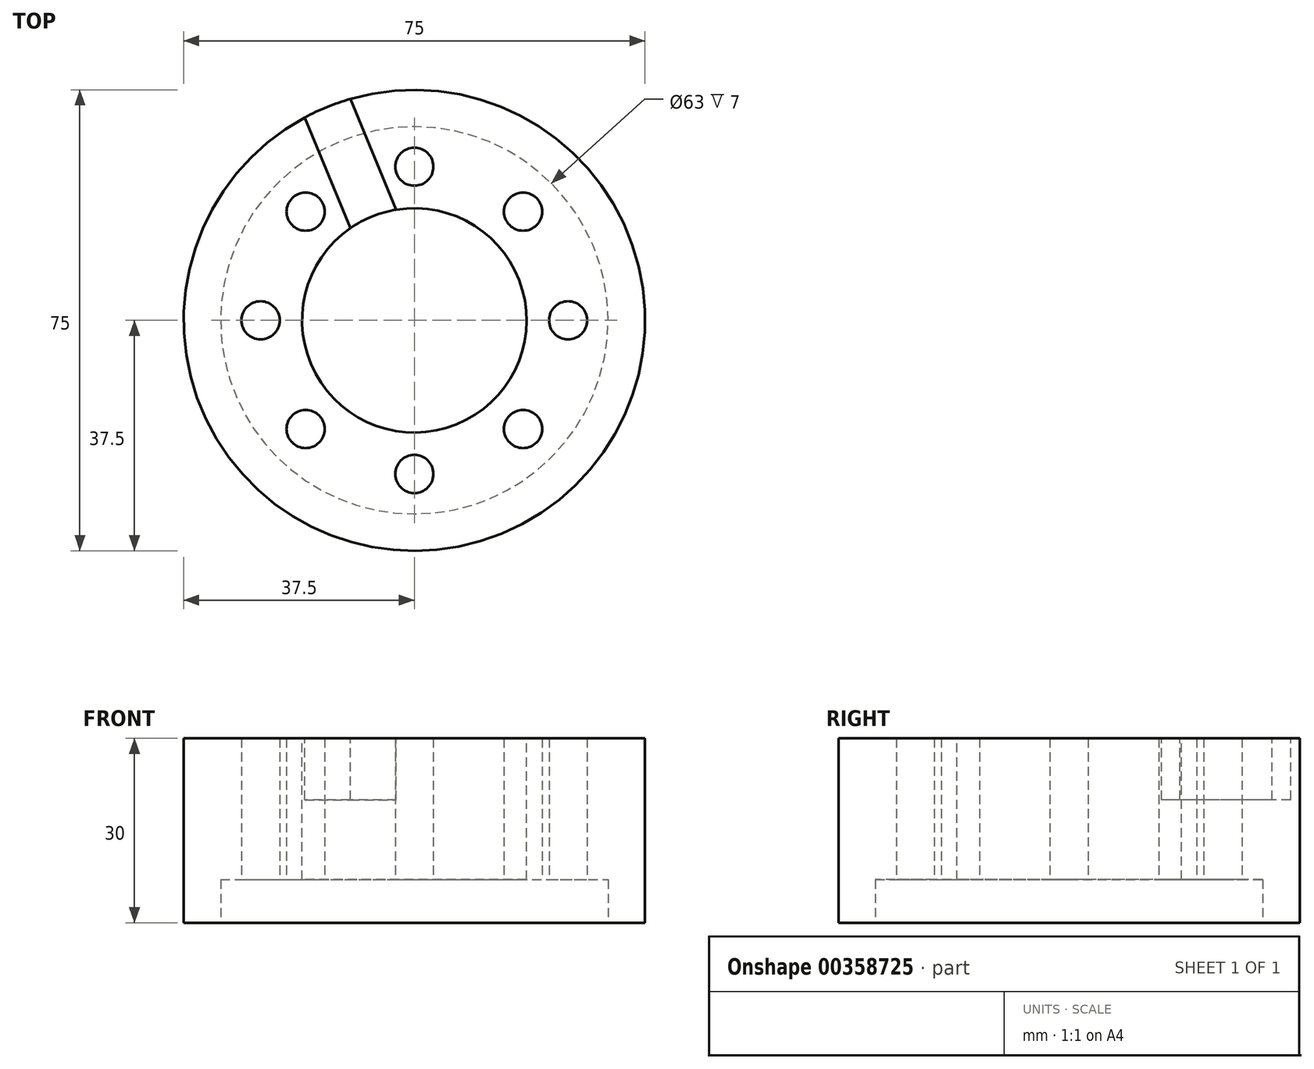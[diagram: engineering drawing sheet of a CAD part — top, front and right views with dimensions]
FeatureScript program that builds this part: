
annotation { "Feature Type Name" : "Feature", "Feature Type Description" : "" }
export const myFeature = defineFeature(function(context is Context, id is Id, definition is map)
    precondition{}
    {
        {
            var Q0;
            Q0=qCreatedBy(makeId("Top.planeOp"),FACE);
            var sketch = newSketch(context, id + "F0", { "sketchPlane" : qUnion([Q0])});
            skCircle(sketch, "E0", {"center": v(0, 0) * mm, "radius": 37.5 * mm});
            skSolve(sketch);
        }
        {
            var Q0;
            Q0=makeQuery(id+"F0.imprint","IMPRINT",FACE,{"disambiguationData":[TD([[makeQuery(id+"F0.imprint","IMPRINT",EDGE,{"derivedFrom":sQuery(id+"F0.wireOp",EDGE,"E0")}),1.0]])]});
            extrude(context, id + "F1", {"entities" : qUnion([Q0]), "depth" : 30 * mm});
        }
        {
            var Q0;
            Q0=makeQuery(id+"F1.opExtrude","CAP_FACE",FACE,{"disambiguationData":[OSD([sQuery(id+"F0.wireOp",EDGE,"E0")])],"isStart":true});
            var sketch = newSketch(context, id + "F2", { "sketchPlane" : qUnion([Q0])});
            skCircle(sketch, "E1", {"center": v(0, 0) * mm, "radius": 31.5 * mm});
            skSolve(sketch);
        }
        {
            var Q0;
            Q0=makeQuery(id+"F2.imprint","IMPRINT",FACE,{"disambiguationData":[TD([[makeQuery(id+"F2.imprint","IMPRINT",EDGE,{"derivedFrom":sQuery(id+"F2.wireOp",EDGE,"E1")}),1.0]])]});
            extrude(context, id + "F3", {"entities" : qUnion([Q0]), "operationType" : NewBodyOperationType.REMOVE, "oppositeDirection" : true, "depth" : 7 * mm});
        }
        {
            var Q0;
            Q0=makeQuery(id+"F3.boolean.opBoolean","COPY",FACE,{"derivedFrom":makeQuery(id+"F3.opExtrude","CAP_FACE",FACE,{"disambiguationData":[OSD([sQuery(id+"F2.wireOp",EDGE,"E1")])],"isStart":false})});
            var sketch = newSketch(context, id + "F4", { "sketchPlane" : qUnion([Q0])});
            skCircle(sketch, "E2", {"center": v(25, 0) * mm, "radius": 3.1 * mm});
            skCircle(sketch, "E3.1.0", {"center": v(17.68, 17.68) * mm, "radius": 3.1 * mm});
            skCircle(sketch, "E3.2.0", {"center": v(0, 25) * mm, "radius": 3.1 * mm});
            skCircle(sketch, "E3.3.0", {"center": v(-17.68, 17.68) * mm, "radius": 3.1 * mm});
            skCircle(sketch, "E3.4.0", {"center": v(-25, 0) * mm, "radius": 3.1 * mm});
            skCircle(sketch, "E3.5.0", {"center": v(-17.68, -17.68) * mm, "radius": 3.1 * mm});
            skCircle(sketch, "E3.6.0", {"center": v(0, -25) * mm, "radius": 3.1 * mm});
            skCircle(sketch, "E3.7.0", {"center": v(17.68, -17.68) * mm, "radius": 3.1 * mm});
            skPoint(sketch, "E3.center", {"position": v(0, 0) * mm});
            skSolve(sketch);
        }
        {
            var Q0;
            Q0 = qSketchRegion(id + "F4", true);
            extrude(context, id + "F5", {"entities" : qUnion([Q0]), "operationType" : NewBodyOperationType.REMOVE, "endBound" : BoundingType.UP_TO_NEXT, "oppositeDirection" : true, "depth" : 25 * mm});
        }
        {
            var Q0;
            Q0=makeQuery(id+"F1.opExtrude","CAP_FACE",FACE,{"disambiguationData":[OSD([sQuery(id+"F0.wireOp",EDGE,"E0")])],"isStart":false});
            var sketch = newSketch(context, id + "F6", { "sketchPlane" : qUnion([Q0])});
            skCircle(sketch, "E4", {"center": v(0, 0) * mm, "radius": 18.25 * mm});
            skSolve(sketch);
        }
        {
            var Q0;
            Q0=makeQuery(id+"F6.imprint","IMPRINT",FACE,{"disambiguationData":[TD([[makeQuery(id+"F6.imprint","IMPRINT",EDGE,{"derivedFrom":sQuery(id+"F6.wireOp",EDGE,"E4")}),1.0]])]});
            extrude(context, id + "F7", {"entities" : qUnion([Q0]), "operationType" : NewBodyOperationType.REMOVE, "endBound" : BoundingType.UP_TO_NEXT, "oppositeDirection" : true, "depth" : 3 * mm});
        }
        {
            var Q0;
            Q0=makeQuery(id+"F1.opExtrude","CAP_FACE",FACE,{"disambiguationData":[OSD([sQuery(id+"F0.wireOp",EDGE,"E0")])],"isStart":false});
            var sketch = newSketch(context, id + "F8", { "sketchPlane" : qUnion([Q0])});
            skLineSegment(sketch, "E5", {"start": v(0, 0) * mm, "end": v(-18.27, 44.1) * mm, "construction": true});
            skLineSegment(sketch, "E6", {"start": v(-14.07, 44.86) * mm, "end": v(3.93, 1.4) * mm});
            skLineSegment(sketch, "E7", {"start": v(-21.14, 41.03) * mm, "end": v(-4.15, 0) * mm});
            skLineSegment(sketch, "E8", {"start": v(-21.14, 41.03) * mm, "end": v(-14.07, 44.86) * mm});
            skLineSegment(sketch, "E9", {"start": v(-4.15, 0) * mm, "end": v(3.93, 1.4) * mm});
            skSolve(sketch);
        }
        {
            var Q0;
            {var subQ0=sQuery(id+"F8.wireOp",EDGE,"E6");var subQ1=makeQuery(id+"F1.opExtrude","CAP_EDGE",EDGE,{"disambiguationData":[OSD([sQuery(id+"F0.wireOp",EDGE,"E0")])],"isStart":false});var subQ2=makeQuery(id+"F8.imprint","INTERSECT",VERTEX,{"derivedFrom":[subQ1,subQ0]});Q0=makeQuery(id+"F8.imprint","IMPRINT",FACE,{"disambiguationData":[TD([[makeQuery(id+"F8.imprint","IMPRINT",EDGE,{"disambiguationData":[TD([[subQ2,-1.0]])],"derivedFrom":subQ0}),-1.0]])]});}
            extrude(context, id + "F9", {"entities" : qUnion([Q0]), "operationType" : NewBodyOperationType.REMOVE, "oppositeDirection" : true, "depth" : 10 * mm});
        }
    });
